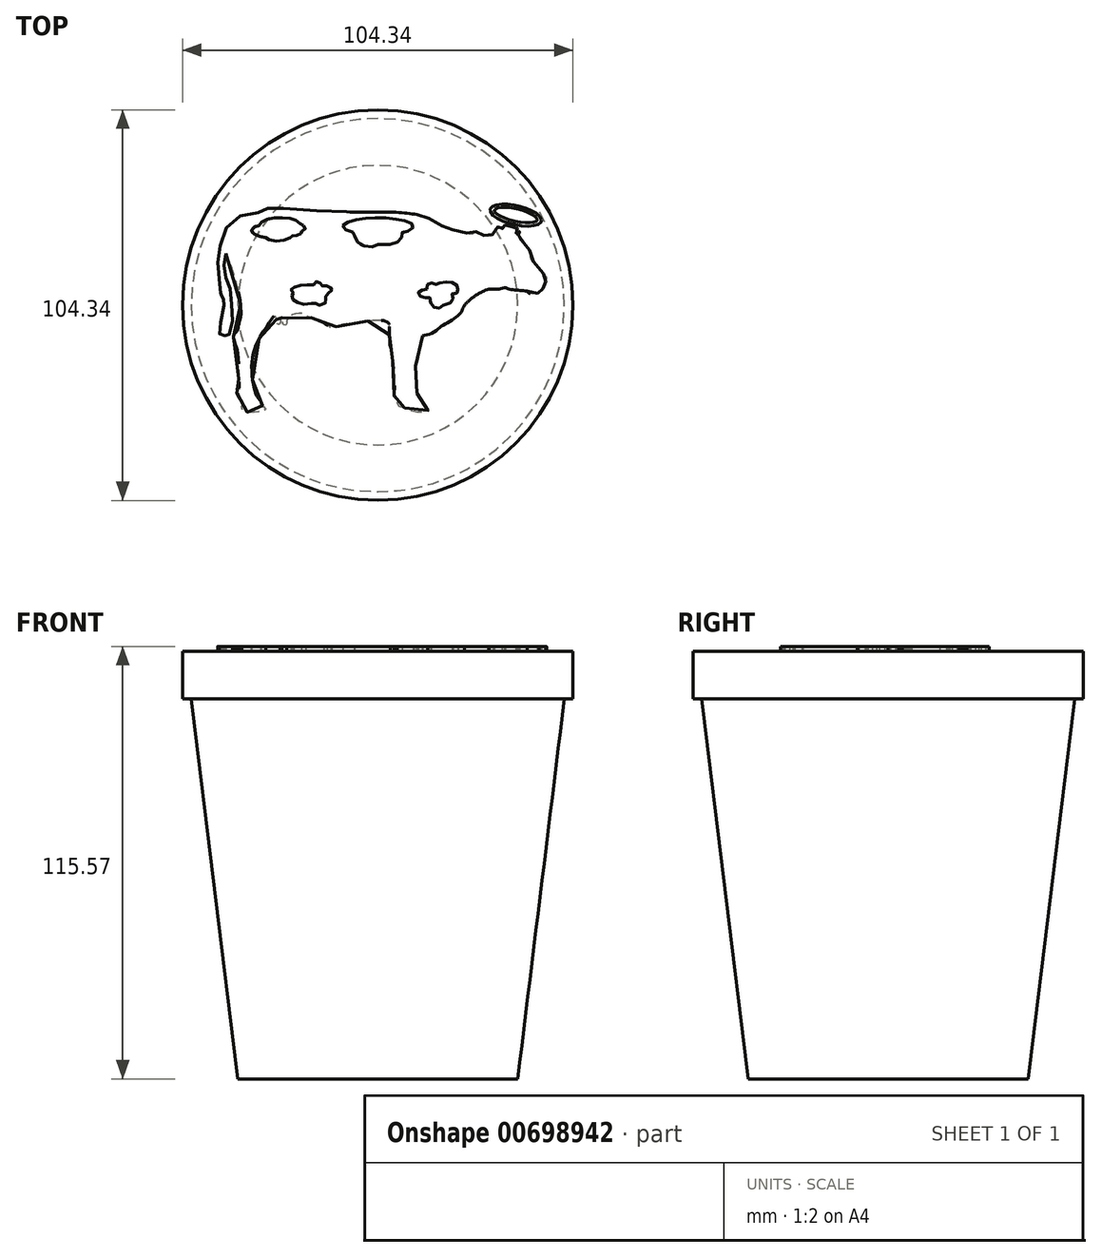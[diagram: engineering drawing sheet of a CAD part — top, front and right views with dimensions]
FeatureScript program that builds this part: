
annotation { "Feature Type Name" : "Feature", "Feature Type Description" : "" }
export const myFeature = defineFeature(function(context is Context, id is Id, definition is map)
    precondition{}
    {
        {
            var Q0;
            Q0=qCreatedBy(makeId("Top.planeOp"),FACE);
            var sketch = newSketch(context, id + "F0", { "sketchPlane" : qUnion([Q0])});
            skCircle(sketch, "E0", {"center": v(0, 0) * mm, "radius": 37.38 * mm});
            skSolve(sketch);
        }
        {
            var Q0;
            Q0 = qSketchRegion(id + "F0", true);
            extrude(context, id + "F1", {"entities" : qUnion([Q0]), "depth" : 101.6 * mm, "offsetDistance" : 25.4 * mm, "hasDraft" : true, "draftAngle" : 7 * degree});
        }
        {
            var Q0;
            Q0=makeQuery(id+"F1.opExtrude","CAP_FACE",FACE,{"disambiguationData":[OSD([sQuery(id+"F0.wireOp",EDGE,"E0")])],"isStart":false});
            var sketch = newSketch(context, id + "F2", { "sketchPlane" : qUnion([Q0])});
            skCircle(sketch, "E1", {"center": v(0, 0) * mm, "radius": 52.17 * mm});
            skSolve(sketch);
        }
        {
            var Q0;
            Q0 = qSketchRegion(id + "F2", true);
            extrude(context, id + "F3", {"entities" : qUnion([Q0]), "operationType" : NewBodyOperationType.ADD, "depth" : 12.7 * mm, "offsetDistance" : 25.4 * mm});
        }
        {
            var Q0;
            Q0=makeQuery(id+"F3.opExtrude","CAP_FACE",FACE,{"disambiguationData":[OSD([sQuery(id+"F2.wireOp",EDGE,"E1")])],"isStart":false});
            var sketch = newSketch(context, id + "F4", { "sketchPlane" : qUnion([Q0])});
            skFitSpline(sketch, "E2", {"points": [v(10.45, 24.2) * mm, v(11, 24.1) * mm, v(11.92, 23.79) * mm, v(12.84, 23.47) * mm, v(13.8, 23.05) * mm, v(15.05, 22.38) * mm, v(16.88, 21.22) * mm, v(17.23, 21.16) * mm, v(17.97, 20.97) * mm, v(18.8, 20.8) * mm, v(19.16, 20.63) * mm, v(19.82, 20.27) * mm, v(20.94, 19.99) * mm, v(22.25, 19.65) * mm, v(23.48, 19.33) * mm, v(24.3, 19.15) * mm, v(25.17, 18.96) * mm, v(25.32, 19.14) * mm, v(25.61, 19.39) * mm, v(26.08, 19.58) * mm, v(26.67, 19.6) * mm, v(27.14, 19.47) * mm, v(27.64, 19.23) * mm, v(28.02, 19) * mm, v(28.23, 18.72) * mm, v(28.55, 18.7) * mm, v(29, 18.58) * mm, v(29.31, 18.52) * mm, v(29.7, 18.5) * mm, v(30.26, 18.63) * mm, v(30.83, 19.07) * mm, v(30.85, 19.26) * mm, v(31.06, 20.02) * mm, v(31.3, 20.36) * mm, v(31.61, 20.64) * mm, v(32.3, 21.06) * mm, v(32.45, 21.07) * mm, v(32.8, 20.76) * mm, v(33.08, 20.4) * mm, v(33.25, 20.16) * mm, v(33.31, 20.27) * mm, v(33.34, 20.48) * mm, v(33.36, 20.82) * mm, v(33.36, 21.07) * mm, v(33.55, 20.83) * mm, v(33.7, 20.8) * mm, v(33.95, 21.06) * mm, v(34, 21.19) * mm, v(34, 21.4) * mm, v(34.11, 21.59) * mm, v(34.2, 21.68) * mm, v(34.24, 21.6) * mm, v(34.23, 21.32) * mm, v(34.64, 21.3) * mm, v(35.13, 21.18) * mm, v(35.77, 20.96) * mm, v(36.25, 20.74) * mm, v(36.6, 20.55) * mm, v(36.85, 20.38) * mm, v(36.94, 20.47) * mm, v(37.1, 20.58) * mm, v(37.3, 20.6) * mm, v(37.39, 20.5) * mm, v(37.4, 20.35) * mm, v(37.33, 20.19) * mm, v(37.24, 19.96) * mm, v(37.13, 19.7) * mm, v(37.04, 19.53) * mm, v(36.94, 19.31) * mm, v(37.01, 19.2) * mm, v(37.13, 19.12) * mm, v(37.22, 19.03) * mm, v(37.3, 19) * mm, v(37.35, 19.09) * mm, v(37.29, 19.21) * mm, v(37.28, 19.32) * mm, v(37.3, 19.41) * mm, v(37.4, 19.5) * mm, v(37.66, 19.66) * mm, v(37.81, 19.7) * mm, v(37.93, 19.66) * mm, v(37.97, 19.46) * mm, v(37.95, 19.27) * mm, v(37.9, 19.17) * mm, v(37.84, 19.1) * mm, v(37.72, 18.98) * mm, v(37.63, 18.96) * mm, v(37.6, 18.84) * mm, v(37.63, 18.68) * mm, v(37.83, 18.36) * mm, v(38.06, 17.77) * mm, v(38.33, 17.4) * mm, v(38.7, 16.93) * mm, v(39.04, 16.62) * mm, v(39.35, 16.38) * mm, v(39.71, 15.98) * mm, v(40.14, 15.5) * mm, v(40.45, 15.12) * mm, v(40.55, 14.54) * mm, v(40.67, 13.3) * mm, v(40.93, 12.28) * mm, v(41.1, 12.06) * mm, v(41.72, 11.44) * mm, v(42.1, 10.92) * mm, v(42.86, 9.84) * mm, v(44.4, 8.23) * mm, v(44.9, 7.58) * mm, v(45.05, 7.25) * mm, v(45.05, 6.99) * mm, v(44.96, 6.92) * mm, v(44.91, 6.53) * mm, v(44.96, 6.03) * mm, v(45, 5.68) * mm, v(44.87, 5.37) * mm, v(44.57, 5.11) * mm, v(44.24, 4.85) * mm, v(44.1, 4.46) * mm, v(43.93, 4.15) * mm, v(43.67, 3.91) * mm, v(43.3, 3.8) * mm, v(43.1, 3.8) * mm, v(43.1, 3.45) * mm, v(42.54, 3.1) * mm, v(41.64, 2.93) * mm, v(40.66, 3.08) * mm, v(40.2, 3.34) * mm, v(39.96, 3.71) * mm], "startDerivative": vector(54.85, -7.68) * mm, "endDerivative": vector(-25.25, 48.33) * mm});
            skFitSpline(sketch, "E3", {"points": [v(29.65, 4.33) * mm, v(30.27, 4.23) * mm, v(31.66, 4.26) * mm, v(32.86, 4.4) * mm, v(34.02, 4.72) * mm, v(34.38, 4.56) * mm, v(34.96, 4.26) * mm, v(36.32, 4.1) * mm, v(37.52, 3.97) * mm, v(38.6, 3.88) * mm, v(39.96, 3.71) * mm], "startDerivative": vector(6.9, -1.57) * mm, "endDerivative": vector(12.14, -1.54) * mm});
            skFitSpline(sketch, "E4", {"points": [v(23.11, 0) * mm, v(23.7, 0.6) * mm, v(24.44, 1.22) * mm, v(25.48, 2.13) * mm, v(26.38, 2.78) * mm, v(27.52, 3.42) * mm, v(29.65, 4.33) * mm], "startDerivative": vector(4.16, 4.63) * mm, "endDerivative": vector(10.3, 4.1) * mm});
            skFitSpline(sketch, "E5", {"points": [v(11.96, -8.2) * mm, v(12.97, -8) * mm, v(14.24, -7.6) * mm, v(15.4, -6.96) * mm, v(16.3, -6.24) * mm, v(17.01, -5.66) * mm, v(17.9, -5.11) * mm, v(19, -4.45) * mm, v(20.3, -3.67) * mm, v(21.2, -2.98) * mm, v(22.06, -2.11) * mm, v(22.46, -1.5) * mm, v(22.72, -0.76) * mm, v(23.11, 0) * mm], "startDerivative": vector(13.1, 2.34) * mm, "endDerivative": vector(6.3, 10.9) * mm});
            skFitSpline(sketch, "E6", {"points": [v(11.96, -8.2) * mm, v(11.48, -10.25) * mm, v(11.16, -11.74) * mm, v(10.91, -13.4) * mm, v(10.83, -14.32) * mm, v(10.51, -15.17) * mm, v(10.3, -15.82) * mm, v(9.87, -16.86) * mm, v(9.9, -17.55) * mm, v(9.95, -18.6) * mm, v(10.07, -20.13) * mm, v(10.15, -20.5) * mm, v(10.39, -21.62) * mm, v(10.51, -22.67) * mm, v(10.51, -23.6) * mm, v(10.6, -24.37) * mm, v(10.95, -24.73) * mm, v(11.32, -25.21) * mm, v(11.96, -26.1) * mm, v(11.96, -26.34) * mm, v(12.3, -26.58) * mm, v(13.01, -27.27) * mm, v(13.41, -27.71) * mm, v(13.41, -28.04) * mm, v(13.33, -28.48) * mm, v(12.3, -28.68) * mm, v(10.55, -28.64) * mm, v(9.34, -28.44) * mm, v(8.3, -28.04) * mm, v(7.77, -27.91) * mm, v(7.32, -27.91) * mm, v(7.2, -27.43) * mm, v(6.92, -27.43) * mm, v(6.32, -27.23) * mm, v(5.6, -27.03) * mm, v(5.39, -26.66) * mm, v(5.19, -25.86) * mm, v(5.1, -25.53) * mm, v(5.43, -25.1) * mm, v(5.5, -25.01) * mm, v(5.03, -24.69) * mm, v(4.5, -24.49) * mm, v(4.46, -22.1) * mm, v(4.54, -19.97) * mm, v(4.54, -18.2) * mm, v(4.42, -16.54) * mm, v(4.34, -15.7) * mm, v(4.06, -15) * mm, v(3.7, -14.24) * mm, v(3.45, -13.15) * mm, v(3.45, -12.19) * mm, v(3.61, -11.9) * mm, v(3.41, -11.38) * mm, v(3.21, -10.17) * mm, v(3.17, -8.96) * mm, v(3.09, -7.5) * mm, v(2.87, -4.66) * mm, v(2.52, -4.53) * mm, v(1.71, -4.18) * mm, v(0.68, -4.11) * mm, v(-1.03, -4.08) * mm, v(-2.51, -4.24) * mm, v(-4.25, -4.53) * mm, v(-5.67, -4.73) * mm, v(-9.6, -5.17) * mm, v(-9.77, -5.3) * mm, v(-10.06, -5.53) * mm, v(-10.34, -5.72) * mm, v(-10.87, -5.72) * mm, v(-11.25, -5.76) * mm, v(-11.73, -5.87) * mm, v(-12.3, -5.97) * mm, v(-12.6, -5.97) * mm, v(-12.88, -5.82) * mm, v(-13.47, -5.38) * mm, v(-14.27, -4.89) * mm, v(-14.57, -4.66) * mm, v(-17.6, -3.43) * mm, v(-19.14, -2.82) * mm, v(-20.02, -2.3) * mm, v(-20.63, -2.17) * mm, v(-21.38, -2.17) * mm, v(-22.55, -2.5) * mm, v(-22.97, -2.59) * mm, v(-23.34, -3.1) * mm, v(-23.72, -3.34) * mm, v(-24.28, -3.7) * mm, v(-24.3, -3.87) * mm, v(-24.33, -4.13) * mm, v(-24.34, -4.55) * mm, v(-24.4, -4.89) * mm, v(-24.53, -5.21) * mm, v(-24.67, -5.34) * mm, v(-24.95, -5.37) * mm, v(-25.16, -5.3) * mm, v(-25.38, -4.89) * mm, v(-25.54, -4.14) * mm, v(-25.64, -3.35) * mm, v(-25.67, -3.04) * mm, v(-26, -3.04) * mm, v(-26.03, -3.44) * mm, v(-26.03, -3.88) * mm, v(-26.02, -4.45) * mm, v(-26.18, -5.1) * mm, v(-26.31, -5.22) * mm, v(-26.65, -5.25) * mm, v(-26.88, -4.94) * mm, v(-27.05, -4.5) * mm, v(-27.13, -4.02) * mm, v(-27.16, -3.64) * mm, v(-27.21, -3.21) * mm, v(-27.36, -3.08) * mm, v(-27.55, -2.99) * mm, v(-27.76, -2.92) * mm, v(-28.15, -3.4) * mm, v(-28.67, -4.18) * mm, v(-30.37, -6.76) * mm, v(-32.33, -10.03) * mm, v(-32.94, -11.81) * mm, v(-33.55, -14.44) * mm, v(-33.7, -16.93) * mm, v(-33.5, -19.47) * mm, v(-33.08, -21.92) * mm, v(-32.42, -24.17) * mm, v(-32.15, -24.53) * mm, v(-31.72, -25.07) * mm, v(-31.35, -25.58) * mm, v(-31.14, -26) * mm, v(-31.14, -26.7) * mm, v(-30.87, -26.84) * mm, v(-30.43, -27.23) * mm, v(-30, -27.7) * mm, v(-30.2, -28.26) * mm, v(-31.15, -28.45) * mm, v(-31.99, -28.56) * mm, v(-32.99, -28.67) * mm, v(-33.9, -28.67) * mm, v(-34.88, -28.59) * mm, v(-35.75, -28.59) * mm, v(-36.13, -27.94) * mm, v(-36.4, -27.18) * mm, v(-36.3, -26.58) * mm, v(-36.02, -26.23) * mm, v(-36.18, -26.2) * mm, v(-36.3, -26.2) * mm, v(-36.5, -26.12) * mm, v(-36.54, -25.93) * mm, v(-36.45, -25.82) * mm, v(-36.45, -25.53) * mm, v(-36.67, -25.34) * mm, v(-36.89, -25.31) * mm, v(-37.27, -25.36) * mm, v(-37.1, -25.26) * mm, v(-36.89, -25.07) * mm, v(-36.78, -24.96) * mm, v(-36.91, -24.85) * mm, v(-37.19, -24.82) * mm, v(-37.46, -24.82) * mm, v(-37.08, -24.47) * mm, v(-36.83, -24.04) * mm, v(-36.86, -23.82) * mm, v(-37.21, -23.6) * mm, v(-37.6, -23.52) * mm, v(-38, -23.39) * mm, v(-37.75, -23.25) * mm, v(-37.43, -23.14) * mm, v(-37.27, -22.9) * mm, v(-37.6, -22.87) * mm, v(-37.94, -22.8) * mm, v(-38, -22.68) * mm, v(-37.73, -22.66) * mm, v(-37.48, -22.36) * mm, v(-37.16, -22.22) * mm, v(-37.1, -20.41) * mm, v(-37.1, -18.84) * mm, v(-37.1, -17.57) * mm, v(-37.5, -12.4) * mm, v(-37.9, -10.8) * mm, v(-38.57, -8.66) * mm, v(-38.5, -8.14) * mm, v(-38.07, -7.3) * mm, v(-37.47, -6.7) * mm, v(-37.14, -5.11) * mm, v(-36.6, -2.77) * mm, v(-36.6, -0.88) * mm, v(-37.06, 2.67) * mm, v(-38.04, 6.75) * mm, v(-39.03, 10) * mm, v(-40.61, 13.86) * mm], "startDerivative": vector(-58.8, -246.14) * mm, "endDerivative": vector(-140.23, 321.3) * mm});
            skFitSpline(sketch, "E7", {"points": [v(10.45, 24.2) * mm, v(7.28, 24.63) * mm, v(3, 24.89) * mm, v(-3.08, 24.89) * mm, v(-8.3, 24.93) * mm], "startDerivative": vector(-14.86, 2.31) * mm, "endDerivative": vector(-19.06, 0.26) * mm});
            skFitSpline(sketch, "E8", {"points": [v(-8.3, 24.93) * mm, v(-14.89, 25.15) * mm, v(-24.6, 25.9) * mm, v(-27, 26) * mm, v(-29.05, 26) * mm, v(-29.91, 25.69) * mm, v(-30.63, 24.87) * mm, v(-31.2, 24.82) * mm, v(-32.78, 24.62) * mm, v(-35.69, 24.2) * mm, v(-37.99, 23.29) * mm, v(-39.93, 21.55) * mm, v(-41.62, 17.87) * mm, v(-42.08, 16.03) * mm, v(-42.49, 14.7) * mm, v(-42.8, 12.4) * mm, v(-42.63, 7.7) * mm, v(-42.29, 5.39) * mm, v(-42.29, 3.26) * mm, v(-42.23, 3.12) * mm, v(-42.08, 3.04) * mm, v(-42.03, 3.18) * mm, v(-42, 3.39) * mm, v(-41.9, 3.3) * mm, v(-41.88, 3.07) * mm, v(-41.88, 2.78) * mm, v(-41.9, 2.55) * mm, v(-41.87, 2.45) * mm, v(-41.76, 2.51) * mm, v(-41.66, 2.54) * mm, v(-41.61, 2.45) * mm, v(-41.67, 2.3) * mm, v(-41.64, 2.07) * mm, v(-41.5, 1.98) * mm, v(-41.41, 2.07) * mm, v(-41.27, 1.9) * mm, v(-41.27, 1.44) * mm, v(-41.27, 1.03) * mm, v(-41.27, 0.62) * mm, v(-41.27, 0.34) * mm, v(-41.08, 0.36) * mm, v(-41.13, 0) * mm, v(-41.22, -0.44) * mm, v(-41.9, -3.85) * mm, v(-42.2, -5.65) * mm, v(-42.36, -6.89) * mm, v(-42.36, -7.52) * mm, v(-42.17, -7.85) * mm, v(-41.75, -8.18) * mm, v(-41.37, -8.24) * mm, v(-40.98, -7.83) * mm, v(-40.84, -8.16) * mm, v(-40.61, -8.57) * mm, v(-40.35, -8.54) * mm, v(-40.1, -8.21) * mm, v(-39.9, -7.74) * mm, v(-39.52, -7.83) * mm, v(-39.03, -7.27) * mm, v(-38.8, -4.93) * mm, v(-38.78, -2.23) * mm, v(-39.03, -0.43) * mm, v(-39.27, 2.24) * mm, v(-39.33, 3.62) * mm, v(-39.63, 5.25) * mm, v(-40.07, 6.35) * mm, v(-40.48, 6.98) * mm, v(-40.83, 7.95) * mm, v(-41.05, 9) * mm, v(-41.11, 10.39) * mm, v(-41.03, 11.28) * mm, v(-40.91, 12.66) * mm, v(-40.61, 13.86) * mm], "startDerivative": vector(-159.34, 2.06) * mm, "endDerivative": vector(21.88, 71.83) * mm});
            skFitSpline(sketch, "E9", {"points": [v(-17.08, 5.45) * mm, v(-18.28, 5.48) * mm, v(-19.94, 5.37) * mm, v(-21.46, 5.08) * mm, v(-22.59, 4.7) * mm, v(-23.15, 4.25) * mm, v(-23.2, 4) * mm, v(-22.99, 3.53) * mm, v(-22.45, 3.2) * mm, v(-22.67, 3.05) * mm, v(-22.93, 2.6) * mm, v(-22.93, 1.98) * mm, v(-22.5, 1.31) * mm, v(-21.46, 0.72) * mm, v(-20.18, 0.38) * mm, v(-18.68, 0.24) * mm, v(-16.97, 0.62) * mm, v(-16.68, 0.46) * mm, v(-16.28, 0.3) * mm, v(-15.8, 0) * mm, v(-14.6, 0.24) * mm, v(-13.69, 0.9) * mm, v(-13.66, 1.34) * mm, v(-14.4, 1.95) * mm, v(-14.06, 2.22) * mm, v(-13.72, 2.91) * mm, v(-13.26, 3.13) * mm, v(-12.3, 3.72) * mm, v(-12.4, 4.09) * mm, v(-12.57, 4.25) * mm, v(-12.57, 4.6) * mm, v(-12.97, 4.97) * mm, v(-13.74, 5.21) * mm, v(-14.38, 5.26) * mm, v(-14.94, 5.18) * mm, v(-15.1, 5.45) * mm, v(-15.48, 5.96) * mm, v(-16.07, 6.28) * mm, v(-16.57, 6.25) * mm, v(-17, 5.77) * mm, v(-17.08, 5.45) * mm]});
            skFitSpline(sketch, "E10", {"points": [v(13.12, 4.3) * mm, v(13.04, 4.78) * mm, v(13.35, 5.57) * mm, v(13.9, 5.86) * mm, v(14.41, 5.95) * mm, v(15.11, 5.86) * mm, v(15.64, 5.48) * mm, v(15.98, 5.7) * mm, v(16.85, 6.07) * mm, v(18.16, 6.24) * mm, v(19.39, 6.2) * mm, v(20.36, 5.86) * mm, v(21.1, 5.3) * mm, v(21.42, 4.74) * mm, v(21.38, 4.13) * mm, v(21.46, 3.9) * mm, v(21.36, 3.53) * mm, v(20.79, 3.15) * mm, v(19.81, 2.98) * mm, v(19.98, 2.69) * mm, v(20.1, 1.92) * mm, v(19.85, 1) * mm, v(19.24, 0.44) * mm, v(18.71, 0.25) * mm, v(18.03, 0.2) * mm, v(17.63, 0.23) * mm, v(17.44, 0) * mm, v(16.97, -0.53) * mm, v(16.34, -0.85) * mm, v(15.4, -0.79) * mm, v(14.64, -0.32) * mm, v(14.18, 0.46) * mm, v(14.18, 1.7) * mm, v(13.82, 1.99) * mm, v(13.18, 2.03) * mm, v(12.44, 2.03) * mm, v(11.43, 2.37) * mm, v(11, 2.7) * mm, v(10.81, 3.2) * mm, v(11, 3.62) * mm, v(11.74, 4.02) * mm, v(12.4, 4.19) * mm, v(13.12, 4.3) * mm]});
            skFitSpline(sketch, "E11", {"points": [v(-9.36, 21.25) * mm, v(-8.94, 21.73) * mm, v(-7.98, 22.21) * mm, v(-6.42, 22.67) * mm, v(-4.72, 22.98) * mm, v(-2.38, 23.23) * mm, v(-0.46, 23.29) * mm, v(2.12, 23.29) * mm, v(4.55, 23.06) * mm, v(6.27, 22.78) * mm, v(7.77, 22.41) * mm, v(8.96, 21.87) * mm, v(9.4, 21.42) * mm, v(9.46, 20.94) * mm, v(9.15, 20.4) * mm, v(8.62, 20.07) * mm, v(7.94, 19.75) * mm, v(7.2, 19.58) * mm, v(6.5, 19.39) * mm, v(6.47, 19.1) * mm, v(6.44, 18.45) * mm, v(6.1, 17.72) * mm, v(5.45, 17.07) * mm, v(4.52, 16.56) * mm, v(3.02, 16.2) * mm, v(2.09, 16.16) * mm, v(1.15, 16.22) * mm, v(0.5, 16.45) * mm, v(0, 16.16) * mm, v(-0.71, 15.8) * mm, v(-1.98, 15.57) * mm, v(-3.28, 15.71) * mm, v(-4.64, 16.25) * mm, v(-5.66, 17.18) * mm, v(-6.05, 18) * mm, v(-6.25, 18.85) * mm, v(-6.25, 19.33) * mm, v(-6.79, 19.47) * mm, v(-7.9, 19.81) * mm, v(-9.02, 20.43) * mm, v(-9.33, 20.91) * mm, v(-9.36, 21.25) * mm]});
            skFitSpline(sketch, "E12", {"points": [v(-31.65, 21.26) * mm, v(-31.52, 21.73) * mm, v(-30.64, 22.48) * mm, v(-28.92, 23.12) * mm, v(-26.68, 23.35) * mm, v(-24.05, 23.25) * mm, v(-22.42, 22.88) * mm, v(-21.34, 22.4) * mm, v(-20.63, 21.63) * mm, v(-20.16, 21.43) * mm, v(-19.45, 20.99) * mm, v(-19.35, 20.45) * mm, v(-19.69, 20.04) * mm, v(-20.43, 19.7) * mm, v(-20.43, 19.5) * mm, v(-20.67, 19.13) * mm, v(-21.48, 18.69) * mm, v(-22.36, 18.45) * mm, v(-22.93, 18.55) * mm, v(-23.07, 18.25) * mm, v(-23.78, 17.8) * mm, v(-25.5, 17.24) * mm, v(-28.07, 17.27) * mm, v(-29.6, 17.78) * mm, v(-30, 18.08) * mm, v(-30.94, 18.25) * mm, v(-32.74, 18.86) * mm, v(-33.68, 19.7) * mm, v(-33.72, 19.97) * mm, v(-33.28, 20.62) * mm, v(-32.57, 21.06) * mm, v(-31.65, 21.26) * mm]});
            skFitSpline(sketch, "E13", {"points": [v(31.29, 25.66) * mm, v(31.76, 25.93) * mm, v(32.53, 26.08) * mm, v(33.74, 26.16) * mm, v(34.95, 26.1) * mm, v(36.41, 25.88) * mm, v(37.95, 25.54) * mm, v(39.63, 25.02) * mm, v(40.82, 24.47) * mm, v(41.73, 23.88) * mm, v(42.43, 23.29) * mm, v(42.58, 22.8) * mm, v(42.5, 22.57) * mm, v(42.13, 22.35) * mm, v(41.36, 22.15) * mm, v(40.37, 22.05) * mm, v(38.64, 22.15) * mm, v(36.68, 22.47) * mm, v(34.56, 23.06) * mm, v(33.07, 23.66) * mm, v(32.16, 24.15) * mm, v(31.36, 24.77) * mm, v(31.12, 25.32) * mm, v(31.29, 25.66) * mm]});
            skFitSpline(sketch, "E14", {"points": [v(30.6, 26.38) * mm, v(31.46, 26.73) * mm, v(33.17, 26.97) * mm, v(34.98, 26.97) * mm, v(37.03, 26.65) * mm, v(39.04, 26.1) * mm, v(40.8, 25.41) * mm, v(42.3, 24.6) * mm, v(43.17, 23.83) * mm, v(43.64, 23.19) * mm, v(43.76, 22.6) * mm, v(43.66, 22.27) * mm, v(43.3, 21.88) * mm, v(42.55, 21.5) * mm, v(41.44, 21.2) * mm, v(39.36, 21.1) * mm, v(37.2, 21.4) * mm, v(35.1, 21.88) * mm, v(33.15, 22.6) * mm, v(31.36, 23.56) * mm, v(30.42, 24.4) * mm, v(30, 25.22) * mm, v(30, 25.59) * mm, v(30.15, 25.93) * mm, v(30.6, 26.38) * mm]});
            skSolve(sketch);
        }
        {
            var Q0;
            Q0 = qSketchRegion(id + "F4", true);
            extrude(context, id + "F5", {"entities" : qUnion([Q0]), "operationType" : NewBodyOperationType.ADD, "depth" : 1.27 * mm, "offsetDistance" : 25.4 * mm});
        }
    });
